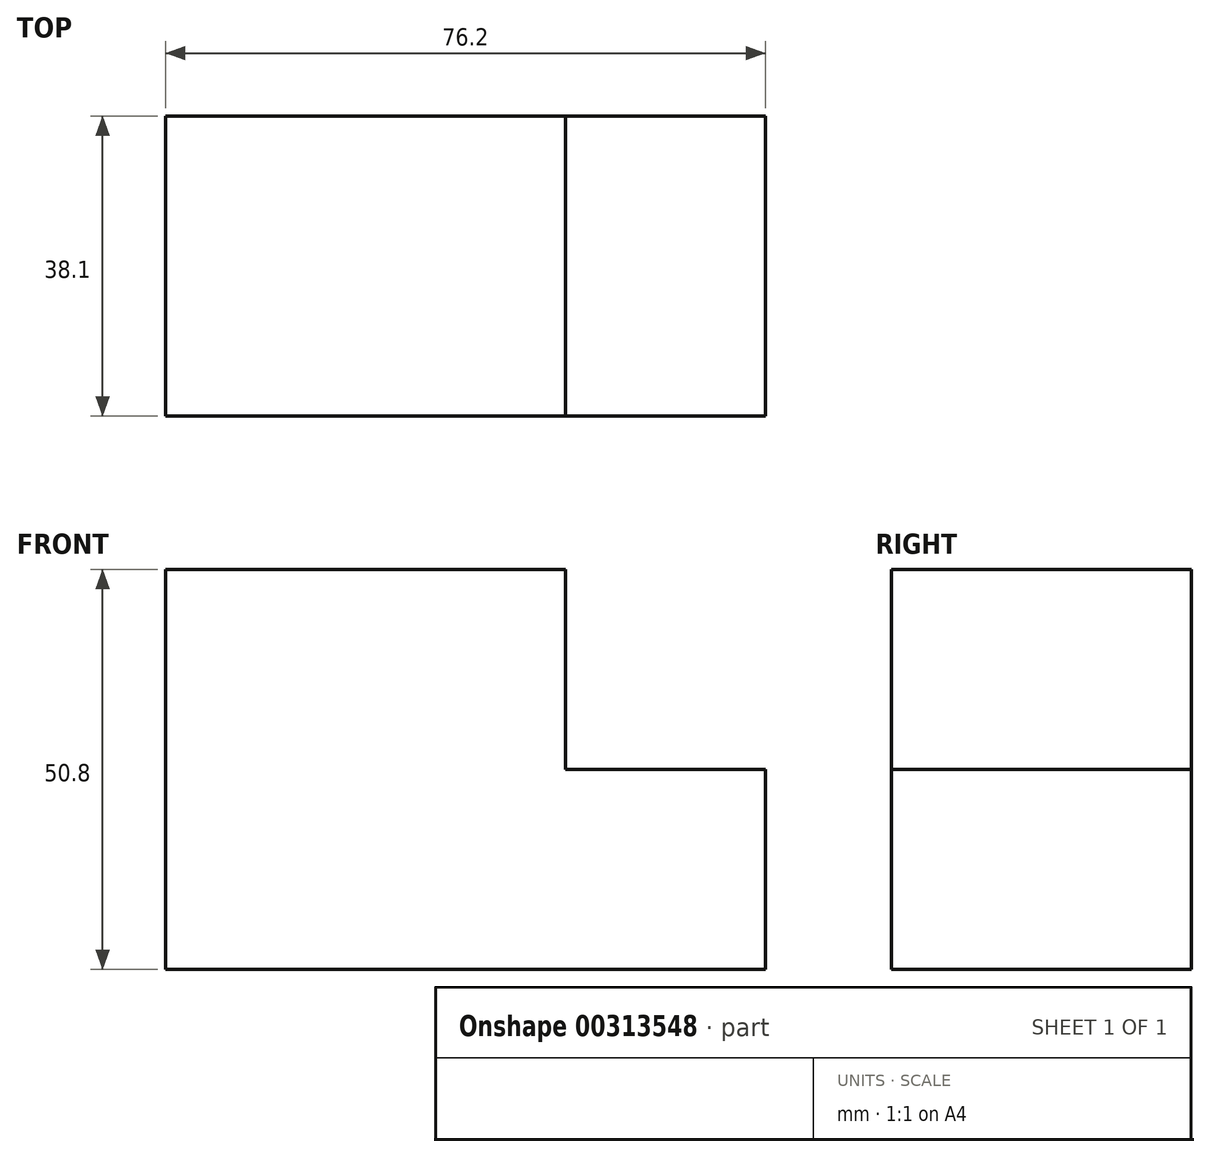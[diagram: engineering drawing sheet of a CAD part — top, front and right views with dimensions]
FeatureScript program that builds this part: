
annotation { "Feature Type Name" : "Feature", "Feature Type Description" : "" }
export const myFeature = defineFeature(function(context is Context, id is Id, definition is map)
    precondition{}
    {
        {
            var Q0;
            Q0=qCreatedBy(makeId("Front.planeOp"),FACE);
            var sketch = newSketch(context, id + "F0", { "sketchPlane" : qUnion([Q0])});
            skLineSegment(sketch, "E0", {"start": v(-36.28, -47.1) * mm, "end": v(39.92, -47.1) * mm});
            skLineSegment(sketch, "E1", {"start": v(39.92, -47.1) * mm, "end": v(39.92, -21.7) * mm});
            skLineSegment(sketch, "E2", {"start": v(39.92, -21.7) * mm, "end": v(14.52, -21.7) * mm});
            skLineSegment(sketch, "E3", {"start": v(14.52, -21.7) * mm, "end": v(14.52, 3.7) * mm});
            skLineSegment(sketch, "E4", {"start": v(14.52, 3.7) * mm, "end": v(-36.28, 3.7) * mm});
            skLineSegment(sketch, "E5", {"start": v(-36.28, 3.7) * mm, "end": v(-36.28, -47.1) * mm});
            skSolve(sketch);
        }
        {
            var Q0;
            Q0=makeQuery(id+"F0.imprint","IMPRINT",FACE,{"disambiguationData":[TD([[makeQuery(id+"F0.imprint","IMPRINT",EDGE,{"derivedFrom":sQuery(id+"F0.wireOp",EDGE,"E0")}),1.0]])]});
            extrude(context, id + "F1", {"entities" : qUnion([Q0]), "depth" : 38.1 * mm});
        }
    });
